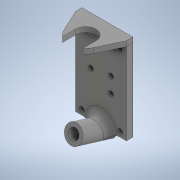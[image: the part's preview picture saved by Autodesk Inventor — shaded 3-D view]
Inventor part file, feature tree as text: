
AUTODESK INVENTOR PART (.ipt)
format: ipt  version: 2022 (Build 260153000, 153)  size: 358,912 bytes
history: native  units: mm
features: other x18, sketch x10, extrude x8, reference x7, plane x2, fillet x2, revolve x1, mirror x1, chamfer x1
ambient origin geometry x8: Origin, YZ Plane, XZ Plane, XY Plane, X Axis, Y Axis, Z Axis, Center Point
bodies: Solid1 (feature_tree)
feature tree (50):
  extrude  "Extrusion1"  Depth=4.0mm
  extrude  "Extrusion2"  Depth=4.0mm
  extrude  "Extrusion3"  Depth=4.0mm
  plane  "Work Plane1"
  revolve  "Revolution1"  [1 undecoded]
  extrude  "Extrusion4"  Depth=4.0mm
  extrude  "Extrusion5"  Depth=4.0mm
  fillet  "Fillet1"  Radius=3.0mm
  extrude  "Extrusion6"  Depth=4.0mm
  sketch  "Sketch8"  dims[d17=3.0mm d18=4.0mm]
  fillet  "Fillet2"  Radius=3.0mm
  extrude  "Extrusion7"  Depth=4.0mm
  plane  "Work Plane2"
  extrude  "Extrusion8"  Depth=4.0mm TaperAngle=0.0deg
  mirror  "Mirror1"
  chamfer  "Chamfer1"  Distance=2.0mm
  sketch  "Sketch1"  dims[d0=5.0mm d1=0.0mm d2=4.0mm]
  reference  "Reference1"
  sketch  "Sketch2"  dims[d3=6.0mm d4=4.0mm]
  reference  "Reference3"
  reference  "Reference4"
  reference  "Reference5"
  reference  "Reference6"
  sketch  "Sketch3"  dims[d5=4.0mm d6=6.0mm]
  reference  "Reference7"
  reference  "Reference8"
  sketch  "Sketch4"  dims[d7=0.0mm d8=4.0mm]
  sketch  "Sketch5"  dims[d9=4.0mm d10=4.0mm]
  sketch  "Sketch6"  dims[d11=4.0mm d12=3.0mm d13=3.0mm]
  sketch  "Sketch7"  dims[d14=4.0mm d15=4.0mm d16=3.0mm]
  sketch  "Sketch9"  dims[d19=4.0mm d20=5.0mm d21=0.0mm]
  sketch  "Sketch10"  dims[d23=2.0mm d24=2.0mm d25=6.75mm d26=0.0mm d29=-19.95mm d30=4.0mm d31=0.0mm d32=2.96706mm d33=3.0mm d34=4.1mm d35=360.0deg d36=32.25mm d37=0.0mm d38=32.25mm d39=0.0mm d40=5.0mm d41=32.25mm d42=0.0mm d43=40.0mm d44=45.0mm d45=10.0mm d46=16.0mm d47=12.0mm d48=5.0mm d49=4.0mm d50=0.0mm d51=7.5mm d52=5.0mm d53=7.5mm d54=4.0mm d55=0.0mm d56=2.0mm d57=2.0mm d58=45.0deg]
  other  "toolhead v2.iam"
  other  "MGN9 mount block:1"
  parser-record x2  (decoder bookkeeping rows leaked as tree rows — omitted from the tree; the rows remain in map.json)
  other  "speedyPrinty.iam"
  other  "Y gantry printed v33_1:3"
  other  "GT2 - 20T_Tension Pulley smooth v2:2"
  other  "Component5:1"
  other  "Y gantry printed v33:2"
  other  "GT2 - 20T_Tension Pulley smooth v2:1"
  other  "Front Idlers mounts Left:2"
  other  "Hardware (4):1"
  other  "GT2 20-Tooth Idler Pulley v5 (5) (1):1"
  other  "Pulley (1) (1):2"
  other  "D2HW_C202M:1"
  other  "Tool holder.iam"
  other  "Volcano_Printhead:1"
  other  "E3D-VOLCANO-1.75-MO:2"
note: 2 file-system paths scrubbed to <path> (originals preserved in map.json)
note: 1 required parameter value undecoded (feature->parameter linkage not recoverable at this tier; creation-order binding heuristic only, values carry confidence <= 0.55)
